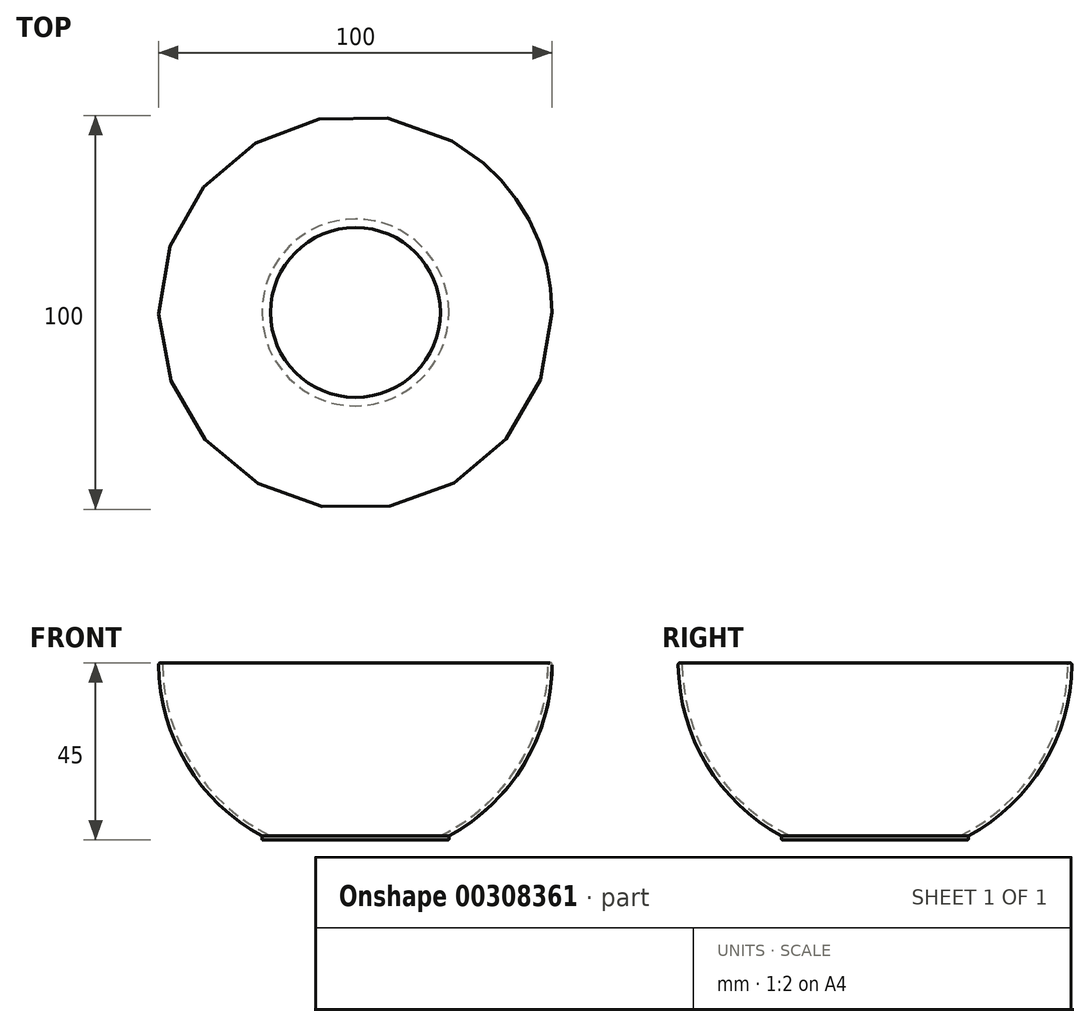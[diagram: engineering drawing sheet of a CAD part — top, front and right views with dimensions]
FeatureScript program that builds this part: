
annotation { "Feature Type Name" : "Feature", "Feature Type Description" : "" }
export const myFeature = defineFeature(function(context is Context, id is Id, definition is map)
    precondition{}
    {
        {
            var Q0;
            Q0=qCreatedBy(makeId("Front.planeOp"),FACE);
            var sketch = newSketch(context, id + "F0", { "sketchPlane" : qUnion([Q0])});
            skArc(sketch, "E0", {"start": v(-50, -0.5) * mm, "mid": v(-42.8, -25.83) * mm, "end": v(-23.75, -44) * mm});
            skArc(sketch, "E1", {"start": v(-49, -0.5) * mm, "mid": v(-41.45, -26.14) * mm, "end": v(-21.56, -44) * mm});
            skLineSegment(sketch, "E2", {"start": v(0, 58.76) * mm, "end": v(0, -72.55) * mm});
            skLineSegment(sketch, "E3", {"start": v(0, -49) * mm, "end": v(0, -44) * mm});
            skLineSegment(sketch, "E4", {"start": v(-23.75, -44) * mm, "end": v(0, -44) * mm});
            skLineSegment(sketch, "E5", {"start": v(-49.5, 0) * mm, "end": v(-49.5, 0) * mm});
            skLineSegment(sketch, "E6.trimOffspring", {"start": v(0, 0) * mm, "end": v(1.21, 0) * mm});
            skLineSegment(sketch, "E7", {"start": v(-23.75, -44) * mm, "end": v(-23.75, -44.75) * mm});
            skLineSegment(sketch, "E8", {"start": v(-23.5, -45) * mm, "end": v(0, -45) * mm});
            skPoint(sketch, "E9.visualSharp", {"position": v(-23.75, -45) * mm});
            skArc(sketch, "E9.filletArc", {"start": v(-23.75, -44.75) * mm, "mid": v(-23.68, -44.93) * mm, "end": v(-23.5, -45) * mm});
            skPoint(sketch, "E10.visualSharp", {"position": v(-50, 0) * mm});
            skArc(sketch, "E10.filletArc", {"start": v(-49.6, -0.01) * mm, "mid": v(-49.89, -0.19) * mm, "end": v(-50, -0.5) * mm});
            skPoint(sketch, "E11.visualSharp", {"position": v(-49, 0) * mm});
            skArc(sketch, "E11.filletArc", {"start": v(-49, -0.5) * mm, "mid": v(-49.19, -0.1) * mm, "end": v(-49.6, -0.01) * mm});
            skSolve(sketch);
        }
        {
            var Q0;
            {var subQ0=sQuery(id+"F0.wireOp",EDGE,"E0");Q0=makeQuery(id+"F0.imprint","IMPRINT",FACE,{"disambiguationData":[TD([[makeQuery(id+"F0.imprint","IMPRINT",EDGE,{"derivedFrom":subQ0}),1.0]])]});}
            var Q1;
            {var subQ0=sQuery(id+"F0.wireOp",EDGE,"E7");Q1=makeQuery(id+"F0.imprint","IMPRINT",FACE,{"disambiguationData":[TD([[makeQuery(id+"F0.imprint","IMPRINT",EDGE,{"derivedFrom":subQ0}),1.0]])]});}
            var Q2;
            Q2=sQuery(id+"F0.wireOp",EDGE,"E2");
            revolve(context, id + "F1", {"entities" : qUnion([Q0, Q1]), "axis" : qUnion([Q2]), "revolveType" : RevolveType.FULL});
        }
    });
